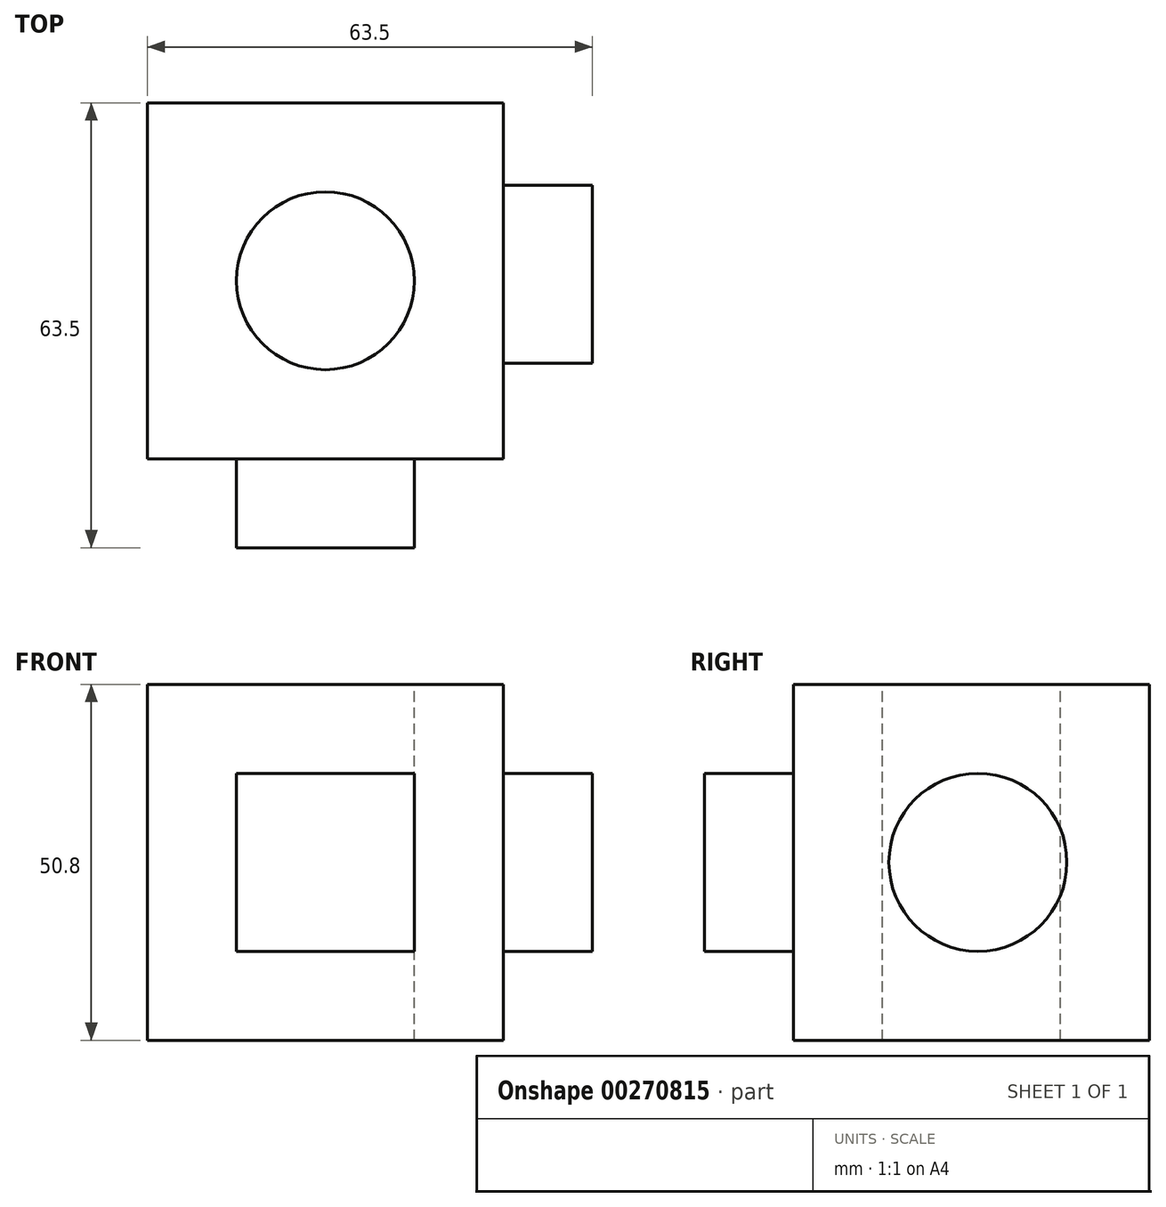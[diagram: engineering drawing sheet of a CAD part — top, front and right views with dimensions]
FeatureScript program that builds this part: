
annotation { "Feature Type Name" : "Feature", "Feature Type Description" : "" }
export const myFeature = defineFeature(function(context is Context, id is Id, definition is map)
    precondition{}
    {
        {
            var Q0;
            Q0=qCreatedBy(makeId("Front.planeOp"),FACE);
            var sketch = newSketch(context, id + "F0", { "sketchPlane" : qUnion([Q0])});
            skLineSegment(sketch, "E0.bottom", {"start": v(0, 0) * mm, "end": v(-50.8, 0) * mm});
            skLineSegment(sketch, "E0.top", {"start": v(0, 50.8) * mm, "end": v(-50.8, 50.8) * mm});
            skLineSegment(sketch, "E0.left", {"start": v(0, 0) * mm, "end": v(0, 50.8) * mm});
            skLineSegment(sketch, "E0.right", {"start": v(-50.8, 0) * mm, "end": v(-50.8, 50.8) * mm});
            skSolve(sketch);
        }
        {
            var Q0;
            Q0 = qSketchRegion(id + "F0", true);
            extrude(context, id + "F1", {"entities" : qUnion([Q0]), "depth" : 50.8 * mm});
        }
        {
            var Q0;
            Q0=makeQuery(id+"F1.opExtrude","SWEPT_FACE",FACE,{"disambiguationData":[OSD([sQuery(id+"F0.wireOp",EDGE,"E0.top")])]});
            var sketch = newSketch(context, id + "F2", { "sketchPlane" : qUnion([Q0])});
            skCircle(sketch, "E1", {"center": v(-25.4, -25.4) * mm, "radius": 12.7 * mm});
            skSolve(sketch);
        }
        {
            var Q0;
            Q0=makeQuery(id+"F2.imprint","IMPRINT",FACE,{"disambiguationData":[TD([[makeQuery(id+"F2.imprint","IMPRINT",EDGE,{"derivedFrom":sQuery(id+"F2.wireOp",EDGE,"E1")}),1.0]])]});
            extrude(context, id + "F3", {"entities" : qUnion([Q0]), "operationType" : NewBodyOperationType.REMOVE, "oppositeDirection" : true, "depth" : 50.8 * mm});
        }
        {
            var Q0;
            Q0=makeQuery(id+"F1.opExtrude","SWEPT_FACE",FACE,{"disambiguationData":[OSD([sQuery(id+"F0.wireOp",EDGE,"E0.left")])]});
            var sketch = newSketch(context, id + "F4", { "sketchPlane" : qUnion([Q0])});
            skCircle(sketch, "E2", {"center": v(-24.48, 25.4) * mm, "radius": 12.7 * mm});
            skSolve(sketch);
        }
        {
            var Q0;
            Q0=makeQuery(id+"F4.imprint","IMPRINT",FACE,{"disambiguationData":[TD([[makeQuery(id+"F4.imprint","IMPRINT",EDGE,{"derivedFrom":sQuery(id+"F4.wireOp",EDGE,"E2")}),1.0]])]});
            extrude(context, id + "F5", {"entities" : qUnion([Q0]), "operationType" : NewBodyOperationType.ADD, "depth" : 12.7 * mm});
        }
        {
            var Q0;
            Q0=makeQuery(id+"F1.opExtrude","CAP_FACE",FACE,{"disambiguationData":[OSD([sQuery(id+"F0.wireOp",EDGE,"E0.bottom"),sQuery(id+"F0.wireOp",EDGE,"E0.top"),sQuery(id+"F0.wireOp",EDGE,"E0.left"),sQuery(id+"F0.wireOp",EDGE,"E0.right")])],"isStart":false});
            var sketch = newSketch(context, id + "F6", { "sketchPlane" : qUnion([Q0])});
            skLineSegment(sketch, "E3.bottom", {"start": v(-12.7, 38.1) * mm, "end": v(-38.1, 38.1) * mm});
            skLineSegment(sketch, "E3.top", {"start": v(-12.7, 12.7) * mm, "end": v(-38.1, 12.7) * mm});
            skLineSegment(sketch, "E3.left", {"start": v(-12.7, 38.1) * mm, "end": v(-12.7, 12.7) * mm});
            skLineSegment(sketch, "E3.right", {"start": v(-38.1, 38.1) * mm, "end": v(-38.1, 12.7) * mm});
            skSolve(sketch);
        }
        {
            var Q0;
            Q0=makeQuery(id+"F6.imprint","IMPRINT",FACE,{"disambiguationData":[TD([[makeQuery(id+"F6.imprint","IMPRINT",EDGE,{"derivedFrom":sQuery(id+"F6.wireOp",EDGE,"E3.bottom")}),1.0]])]});
            extrude(context, id + "F7", {"entities" : qUnion([Q0]), "operationType" : NewBodyOperationType.ADD, "depth" : 12.7 * mm});
        }
    });
